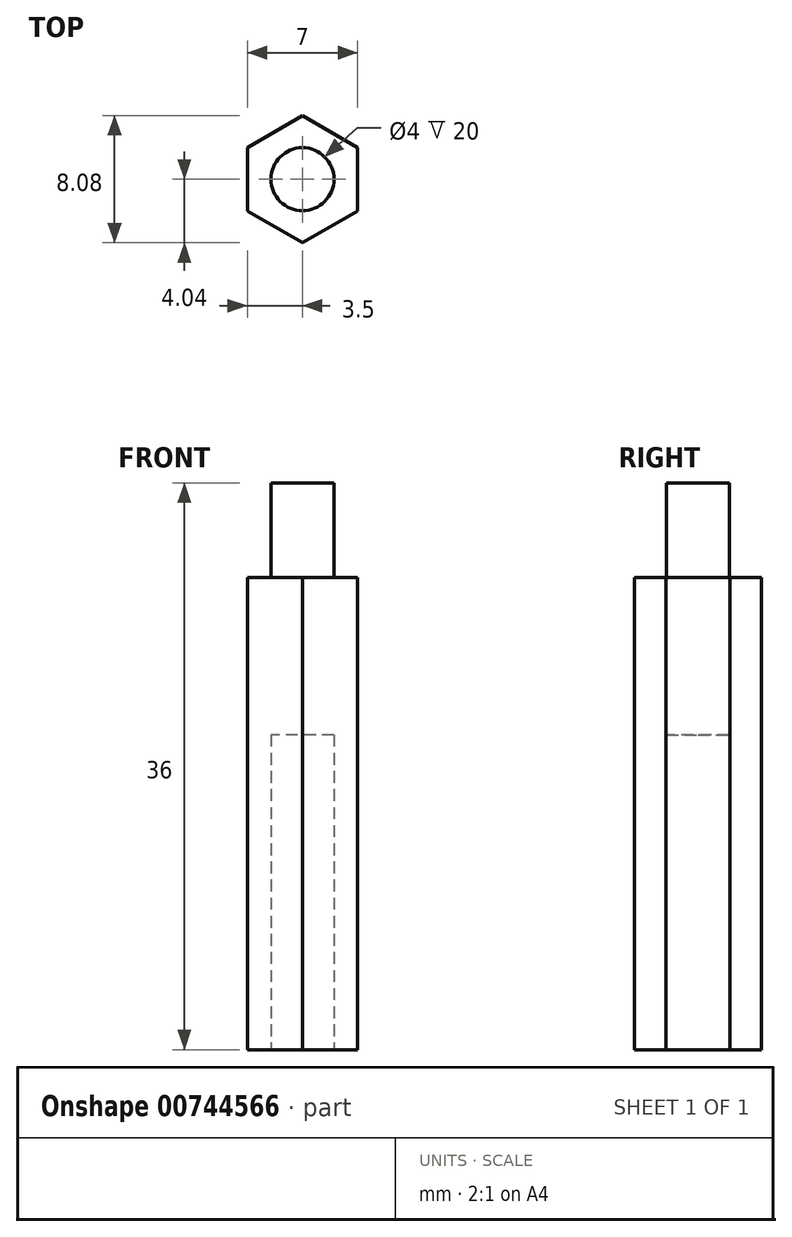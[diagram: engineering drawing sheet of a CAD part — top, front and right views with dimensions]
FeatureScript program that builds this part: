
annotation { "Feature Type Name" : "Feature", "Feature Type Description" : "" }
export const myFeature = defineFeature(function(context is Context, id is Id, definition is map)
    precondition{}
    {
        {
            var Q0;
            Q0=qCreatedBy(makeId("Top.planeOp"),FACE);
            var sketch = newSketch(context, id + "F0", { "sketchPlane" : qUnion([Q0])});
            skCircle(sketch, "E0.cCircle", {"center": v(0, 0) * mm, "radius": 4.04 * mm, "construction": true});
            skLineSegment(sketch, "E0.0", {"start": v(3.5, 2.02) * mm, "end": v(3.5, -2.02) * mm});
            skLineSegment(sketch, "E0.1", {"start": v(3.5, -2.02) * mm, "end": v(0, -4.04) * mm});
            skLineSegment(sketch, "E0.2", {"start": v(0, -4.04) * mm, "end": v(-3.5, -2.02) * mm});
            skLineSegment(sketch, "E0.3", {"start": v(-3.5, -2.02) * mm, "end": v(-3.5, 2.02) * mm});
            skLineSegment(sketch, "E0.4", {"start": v(-3.5, 2.02) * mm, "end": v(0, 4.04) * mm});
            skLineSegment(sketch, "E0.5", {"start": v(0, 4.04) * mm, "end": v(3.5, 2.02) * mm});
            skCircle(sketch, "E1", {"center": v(0, 0) * mm, "radius": 2 * mm});
            skSolve(sketch);
        }
        {
            var Q0;
            Q0=qSketchRegion(id+"F0",true);
            extrude(context, id + "F1", {"entities" : qUnion([Q0]), "depth" : 30 * mm, "offsetDistance" : 25 * mm});
        }
        {
            var Q0;
            Q0=makeQuery(id+"F1.opExtrude","CAP_FACE",FACE,{"disambiguationData":[OSD([sQuery(id+"F0.wireOp",EDGE,"E0.0"),sQuery(id+"F0.wireOp",EDGE,"E0.1"),sQuery(id+"F0.wireOp",EDGE,"E0.2"),sQuery(id+"F0.wireOp",EDGE,"E0.3"),sQuery(id+"F0.wireOp",EDGE,"E0.4"),sQuery(id+"F0.wireOp",EDGE,"E0.5")])],"isStart":false});
            var sketch = newSketch(context, id + "F2", { "sketchPlane" : qUnion([Q0])});
            skCircle(sketch, "E2", {"center": v(0, 0) * mm, "radius": 2 * mm});
            skSolve(sketch);
        }
        {
            var Q0;
            Q0=makeQuery(id+"F2.imprint","IMPRINT",FACE,{"disambiguationData":[TD([[makeQuery(id+"F2.imprint","IMPRINT",EDGE,{"derivedFrom":sQuery(id+"F2.wireOp",EDGE,"E2")}),1.0]])]});
            extrude(context, id + "F3", {"entities" : qUnion([Q0]), "operationType" : NewBodyOperationType.ADD, "depth" : 6 * mm, "offsetDistance" : 25 * mm, "hasSecondDirection" : true, "secondDirectionOppositeDirection" : true, "secondDirectionDepth" : 10 * mm});
        }
    });
